# Revit family: pcfy-p45_160kmg8_50Hz
name_source: partatom
category: 機械設備
units: mm (PartAtom-declared; Revit-internal decimal feet)

## family parameters
OmniClass タイトル = Split System Air Conditioning Units
OmniClass 番号 = 23.75.10.24.21.27.27
パーツ タイプ = 標準
ロード時にボイドで切り取り = いいえ
丸型コネクタ寸法 = 直径を使用
作業面ベース = いいえ
共有 = いいえ
常に垂直 = はい
部屋計算ポイント = はい

## types (8) — shared parameters
Clearance Bottom = 500  [stored 1.64042 ft]
Clearance Front = 1500  [stored 4.92126 ft]
Clearance Left = 270  [stored 0.885827 ft]
Clearance Right = 300  [stored 0.984252 ft]
Clearance Top = 1  [stored 0.00328084 ft]
Depth = 680  [stored 2.23097 ft]
Height = 236
Height_本体 = 230  [stored 0.754593 ft]
IfcExportAs = IfcUnitaryEquipmentType
IfcExportType = AIRCONDITIONINGUNIT
OmniClassCode = 23-33 17 13 11
URL = https://www.mitsubishielectric.co.jp
Uniclass2015Code = Pr_70_65_03_84
Uniclass2015Title = Split coil remote air cooled condensing units
Uniclass2015Version = Systems v1.9
ケーブルサイズ1 = 2 mm
サービススペース = はい
ドレン管径 = 20 mm
ドレン管径 (外径) = 26 mm
ドレン管高さ = 190  [stored 0.62336 ft]
パネルマテリアル = <カテゴリ別>
仕様書バージョン = Version1.0
企業コード = 108420
冷媒ガス管高さ = 126  [stored 0.413386 ft]
冷媒液管長さ = 184  [stored 0.603675 ft]
冷媒液管高さ = 126  [stored 0.413386 ft]
冷媒管径 = 100 mm
冷媒高低圧ガス管径 = 0 mm
分類コード = 50053003221080
加湿給水管径 = 0 mm
参照している仕様書等のバージョン = 公共建築物標準仕様書（機械設備工事編）平成31年度版
吊りボルト_H = 50  [stored 0.164042 ft]
吊り位置Y = 320  [stored 1.04987 ft]
周波数 = 50 Hz
呼称 = 室内機_天井吊(露出)形
始動方式 = 直入
形式 = 天井吊（露出）形
推奨ブレーカー容量 = 15 A
本体マテリアル = <カテゴリ別>
極数 = 1
法定耐用年数 = 6
消費電力_加湿器 = 0.00 kW
消費電力_電気ヒーター = 0.00 kW
点検口 = はい
発停方法 = 付属スイッチ
相 = 1
積算_科目 = 1 空気調和設備
符号 = ACP-CR
製品リリース年月 = 2021年6月30日
製品出荷対象 = 国内
製造元 = 三菱電機株式会社
設置方法 = 天井吊形
設計冷房能力 = 0 kW
設計冷房能力_顕熱 = 0 kW
設計暖房能力 = 0.00 kW
説明 = ビル用マルチ 天吊形室内機
負荷分類 = 3_ファン類
運転質量 = 0.00 kg
電圧 = 200 V
電圧_電気ヒーター = 0 V
zero-valued in all types: Clearance Back, 有効加湿量, 点検口設置範囲, 電源_H

## per-type parameters (varying)
- 天吊_PCFY-P45KMG8: MAX風量=720.0 m³/h; MID風量=660.0 m³/h; MID風量2=600.0 m³/h; MIN風量=540.0 m³/h; Width=960  [stored 3.14961 ft]; モデル=PCFY-P45KMG; 冷媒ガス管径=13 mm; 冷媒ガス管長さ=203  [stored 0.66601 ft]; 冷媒液管径=6 mm; 冷媒管径符号=Ac; 冷房能力=4.5 kW; 吊り位置X=917  [stored 3.00853 ft]; 暖房能力=5.00 kW; 消費電力=0.05 kW; 消費電力_冷房=0.05 kW; 消費電力_暖房=0.04 kW; 製品質量=24.00 kg; 質量=28.80 kg; 電動機出力_送風機=0.09 kW; 音響パワーレベル(dB)=53; 音響パワーレベル（中1）(dB)=51; 音響パワーレベル（中2）(dB)=49; 音響パワーレベル（弱）(dB)=48; 風量=720.0 m³/h; 風量（m3／min）=12; 風量（中1）（m3／min）=11; 風量（中2）（m3／min）=10; 風量（弱）（m3／min）=9
- 天吊_PCFY-P56KMG8: MAX風量=780.0 m³/h; MID風量=720.0 m³/h; MID風量2=660.0 m³/h; MIN風量=600.0 m³/h; Width=960  [stored 3.14961 ft]; モデル=PCFY-P56KMG; 冷媒ガス管径=13 mm; 冷媒ガス管長さ=203  [stored 0.66601 ft]; 冷媒液管径=6 mm; 冷媒管径符号=Ac; 冷房能力=5.6 kW; 吊り位置X=917  [stored 3.00853 ft]; 暖房能力=6.30 kW; 消費電力=0.06 kW; 消費電力_冷房=0.06 kW; 消費電力_暖房=0.05 kW; 製品質量=24.00 kg; 質量=28.80 kg; 電動機出力_送風機=0.09 kW; 音響パワーレベル(dB)=55; 音響パワーレベル（中1）(dB)=53; 音響パワーレベル（中2）(dB)=51; 音響パワーレベル（弱）(dB)=49; 風量=780.0 m³/h; 風量（m3／min）=13; 風量（中1）（m3／min）=12; 風量（中2）（m3／min）=11; 風量（弱）（m3／min）=10
- 天吊_PCFY-P71KMG8: MAX風量=1080.0 m³/h; MID風量=960.0 m³/h; MID風量2=900.0 m³/h; MIN風量=840.0 m³/h; Width=1280  [stored 4.19948 ft]; モデル=PCFY-P71KMG; 冷媒ガス管径=16 mm; 冷媒ガス管長さ=200  [stored 0.656168 ft]; 冷媒液管径=10 mm; 冷媒管径符号=Bd; 冷房能力=7.1 kW; 吊り位置X=1237  [stored 4.0584 ft]; 暖房能力=8.00 kW; 消費電力=0.08 kW; 消費電力_冷房=0.08 kW; 消費電力_暖房=0.07 kW; 製品質量=32.00 kg; 質量=38.40 kg; 電動機出力_送風機=0.10 kW; 音響パワーレベル(dB)=55; 音響パワーレベル（中1）(dB)=54; 音響パワーレベル（中2）(dB)=53; 音響パワーレベル（弱）(dB)=52; 風量=1080.0 m³/h; 風量（m3／min）=18; 風量（中1）（m3／min）=16; 風量（中2）（m3／min）=15; 風量（弱）（m3／min）=14
- 天吊_PCFY-P80KMG8: MAX風量=1080.0 m³/h; MID風量=960.0 m³/h; MID風量2=900.0 m³/h; MIN風量=840.0 m³/h; Width=1280  [stored 4.19948 ft]; モデル=PCFY-P80KMG; 冷媒ガス管径=16 mm; 冷媒ガス管長さ=200  [stored 0.656168 ft]; 冷媒液管径=10 mm; 冷媒管径符号=Bd; 冷房能力=8 kW; 吊り位置X=1237  [stored 4.0584 ft]; 暖房能力=9.00 kW; 消費電力=0.08 kW; 消費電力_冷房=0.08 kW; 消費電力_暖房=0.07 kW; 製品質量=32.00 kg; 質量=38.40 kg; 電動機出力_送風機=0.10 kW; 音響パワーレベル(dB)=55; 音響パワーレベル（中1）(dB)=54; 音響パワーレベル（中2）(dB)=53; 音響パワーレベル（弱）(dB)=52; 風量=1080.0 m³/h; 風量（m3／min）=18; 風量（中1）（m3／min）=16; 風量（中2）（m3／min）=15; 風量（弱）（m3／min）=14
- 天吊_PCFY-P90KMG8: MAX風量=1200.0 m³/h; MID風量=1080.0 m³/h; MID風量2=960.0 m³/h; MIN風量=900.0 m³/h; Width=1280  [stored 4.19948 ft]; モデル=PCFY-P90KMG; 冷媒ガス管径=16 mm; 冷媒ガス管長さ=200  [stored 0.656168 ft]; 冷媒液管径=10 mm; 冷媒管径符号=Bd; 冷房能力=9 kW; 吊り位置X=1237  [stored 4.0584 ft]; 暖房能力=10.00 kW; 消費電力=0.09 kW; 消費電力_冷房=0.09 kW; 消費電力_暖房=0.08 kW; 製品質量=32.00 kg; 質量=38.40 kg; 電動機出力_送風機=0.10 kW; 音響パワーレベル(dB)=58; 音響パワーレベル（中1）(dB)=56; 音響パワーレベル（中2）(dB)=55; 音響パワーレベル（弱）(dB)=54; 風量=1200.0 m³/h; 風量（m3／min）=20; 風量（中1）（m3／min）=18; 風量（中2）（m3／min）=16; 風量（弱）（m3／min）=15
- 天吊_PCFY-P112KMG8: MAX風量=1680.0 m³/h; MID風量=1500.0 m³/h; MID風量2=1320.0 m³/h; MIN風量=1200.0 m³/h; Width=1600  [stored 5.24934 ft]; モデル=PCFY-P112KMG; 冷媒ガス管径=16 mm; 冷媒ガス管長さ=200  [stored 0.656168 ft]; 冷媒液管径=10 mm; 冷媒管径符号=Bd; 冷房能力=11.2 kW; 吊り位置X=1557  [stored 5.10827 ft]; 暖房能力=12.50 kW; 消費電力=0.14 kW; 消費電力_冷房=0.14 kW; 消費電力_暖房=0.13 kW; 製品質量=36.00 kg; 質量=43.20 kg; 電動機出力_送風機=0.16 kW; 音響パワーレベル(dB)=61; 音響パワーレベル（中1）(dB)=59; 音響パワーレベル（中2）(dB)=57; 音響パワーレベル（弱）(dB)=55; 風量=1680.0 m³/h; 風量（m3／min）=28; 風量（中1）（m3／min）=25; 風量（中2）（m3／min）=22; 風量（弱）（m3／min）=20
- 天吊_PCFY-P140KMG8: MAX風量=1860.0 m³/h; MID風量=1620.0 m³/h; MID風量2=1440.0 m³/h; MIN風量=1260.0 m³/h; Width=1600  [stored 5.24934 ft]; モデル=PCFY-P140KMG; 冷媒ガス管径=16 mm; 冷媒ガス管長さ=200  [stored 0.656168 ft]; 冷媒液管径=10 mm; 冷媒管径符号=Bd; 冷房能力=14 kW; 吊り位置X=1557  [stored 5.10827 ft]; 暖房能力=16.00 kW; 消費電力=0.16 kW; 消費電力_冷房=0.16 kW; 消費電力_暖房=0.15 kW; 製品質量=38.00 kg; 質量=45.60 kg; 電動機出力_送風機=0.16 kW; 音響パワーレベル(dB)=63; 音響パワーレベル（中1）(dB)=61; 音響パワーレベル（中2）(dB)=59; 音響パワーレベル（弱）(dB)=57; 風量=1860.0 m³/h; 風量（m3／min）=31; 風量（中1）（m3／min）=27; 風量（中2）（m3／min）=24; 風量（弱）（m3／min）=21
- 天吊_PCFY-P160KMG8: MAX風量=1860.0 m³/h; MID風量=1620.0 m³/h; MID風量2=1440.0 m³/h; MIN風量=1260.0 m³/h; Width=1600  [stored 5.24934 ft]; モデル=PCFY-P160KMG; 冷媒ガス管径=16 mm; 冷媒ガス管長さ=200  [stored 0.656168 ft]; 冷媒液管径=10 mm; 冷媒管径符号=Bd; 冷房能力=16 kW; 吊り位置X=1557  [stored 5.10827 ft]; 暖房能力=18.00 kW; 消費電力=0.19 kW; 消費電力_冷房=0.19 kW; 消費電力_暖房=0.18 kW; 製品質量=39.00 kg; 質量=46.80 kg; 電動機出力_送風機=0.16 kW; 音響パワーレベル(dB)=64; 音響パワーレベル（中1）(dB)=62; 音響パワーレベル（中2）(dB)=60; 音響パワーレベル（弱）(dB)=58; 風量=1860.0 m³/h; 風量（m3／min）=31; 風量（中1）（m3／min）=27; 風量（中2）（m3／min）=24; 風量（弱）（m3／min）=21

note: [stored X ft] marks values corroborated as IEEE doubles in the binary element streams (Revit-internal decimal feet)

## geometry (parser evidence)
native form markers: Blend x4
no freeform markers — native parametric forms only
